FCSTD DOCUMENT  (FreeCAD 0.22R36526 (Git))
Label: card
License: All rights reserved
LicenseURL: http://en.wikipedia.org/wiki/All_rights_reserved
objects: Sketcher::SketchObject×3, PartDesign::Body×1
note: 4 computed .brp shape members not serialized (recipe doc carries the construction recipe); baked Part::Feature solids carry a one-line shape summary decoded from their .brp

FEATURE [Sketcher::SketchObject] Sketch  label="Outline"
  AttachmentSupport = -> [XY_Plane]
  FullyConstrained = true
  MapMode = 5
  sketch-geometry (10):
    g0: LineSegment StartX=-63 StartY=15 StartZ=0 EndX=-63 EndY=-15 EndZ=0
    g1: LineSegment StartX=-61 StartY=-17 StartZ=0 EndX=61 EndY=-17 EndZ=0
    g2: LineSegment StartX=63 StartY=-15 StartZ=0 EndX=63 EndY=15 EndZ=0
    g3: LineSegment StartX=61 StartY=17 StartZ=0 EndX=-61 EndY=17 EndZ=0
    g4: ArcOfCircle CenterX=-61 CenterY=15 CenterZ=0 NormalX=0 NormalY=0 NormalZ=1 AngleXU=0 Radius=2 StartAngle=1.5708 EndAngle=3.14159
    g5: ArcOfCircle CenterX=-61 CenterY=-15 CenterZ=0 NormalX=0 NormalY=0 NormalZ=1 AngleXU=0 Radius=2 StartAngle=3.14159 EndAngle=4.71239
    g6: ArcOfCircle CenterX=61 CenterY=-15 CenterZ=0 NormalX=0 NormalY=0 NormalZ=1 AngleXU=0 Radius=2 StartAngle=4.71239 EndAngle=6.28319
    g7: ArcOfCircle CenterX=61 CenterY=15 CenterZ=0 NormalX=0 NormalY=0 NormalZ=1 AngleXU=0 Radius=2 StartAngle=3.611e-13 EndAngle=1.5708
    g8: GeomPoint X=-63 Y=17 Z=0
    g9: GeomPoint X=63 Y=-17 Z=0
  constraints (23):
    c: Tangent(g0,g4) = -1.5708
    c: Tangent(g0,g5) = -1.5708
    c: Tangent(g1,g5) = -1.5708
    c: Tangent(g1,g6) = -1.5708
    c: Tangent(g2,g6) = -1.5708
    c: Tangent(g2,g7) = -1.5708
    c: Tangent(g3,g7) = -1.5708
    c: Tangent(g3,g4) = -1.5708
    c: Vertical(g0)
    c: Vertical(g2)
    c: Horizontal(g1)
    c: Horizontal(g3)
    c: Equal(g4,g5)
    c: Equal(g5,g6)
    c: Equal(g6,g7)
    c: PointOnObject(g8,g0)
    c: PointOnObject(g8,g3)
    c: PointOnObject(g9,g1)
    c: PointOnObject(g9,g2)
    c: Radius(g5) = 2
    c: DistanceX(g8,g9) = 126
    c: DistanceY(g9,g8) = 34
    c: Symmetric(g8,g9,g-1)
FEATURE [Sketcher::SketchObject] Sketch001  label="VerticalGaps"
  AttachmentSupport = -> [XY_Plane]
  FullyConstrained = false
  MapMode = 5
  sketch-geometry (9):
    g0: LineSegment StartX=-52 StartY=24.2339 StartZ=0 EndX=-52 EndY=-25.7661 EndZ=0
    g1: LineSegment StartX=-39 StartY=24.2339 StartZ=0 EndX=-39 EndY=-25.7661 EndZ=0
    g2: LineSegment StartX=-26 StartY=24.2339 StartZ=0 EndX=-26 EndY=-25.7661 EndZ=0
    g3: LineSegment StartX=-13 StartY=24.2339 StartZ=0 EndX=-13 EndY=-25.7661 EndZ=0
    g4: LineSegment StartX=0 StartY=24.2339 StartZ=0 EndX=0 EndY=-25.7661 EndZ=0
    g5: LineSegment StartX=13 StartY=24.2339 StartZ=0 EndX=13 EndY=-25.7661 EndZ=0
    g6: LineSegment StartX=26 StartY=24.2339 StartZ=0 EndX=26 EndY=-25.7661 EndZ=0
    g7: LineSegment StartX=39 StartY=24.2339 StartZ=0 EndX=39 EndY=-25.7661 EndZ=0
    g8: LineSegment StartX=52 StartY=24.2339 StartZ=0 EndX=52 EndY=-25.7661 EndZ=0
  constraints (35):
    c: Vertical(g0)
    c: Vertical(g1)
    c: Vertical(g2)
    c: Vertical(g3)
    c: DistanceY(g0,g0) = 50
    c: Equal(g0,g1)
    c: Equal(g1,g2)
    c: Equal(g2,g3)
    c: Horizontal(g0,g1)
    c: Horizontal(g1,g2)
    c: Horizontal(g2,g3)
    c: DistanceX(g0,g-1) = 52
    c: DistanceX(g1,g-1) = 39
    c: DistanceX(g2,g-1) = 26
    c: DistanceX(g3,g-1) = 13
    c: Vertical(g4)
    c: Vertical(g5)
    c: Vertical(g6)
    c: Vertical(g7)
    c: Vertical(g8)
    c: Equal(g0,g4)
    c: Equal(g4,g5)
    c: Equal(g5,g6)
    c: Equal(g6,g7)
    c: Equal(g7,g8)
    c: Horizontal(g0,g4)
    c: Horizontal(g4,g5)
    c: Horizontal(g5,g6)
    c: Horizontal(g6,g7)
    c: Horizontal(g7,g8)
    c: DistanceX(g-1,g4) = 0
    c: DistanceX(g-1,g5) = 13
    c: DistanceX(g-1,g6) = 26
    c: DistanceX(g-1,g7) = 39
    c: DistanceX(g-1,g8) = 52
FEATURE [Sketcher::SketchObject] Sketch002  label="HorizontalGaps"
  AttachmentSupport = -> [XY_Plane]
  FullyConstrained = false
  MapMode = 5
  sketch-geometry (5):
    g0: LineSegment StartX=-74.7522 StartY=-11.75 StartZ=0 EndX=75.2478 EndY=-11.75 EndZ=0
    g1: LineSegment StartX=-74.7522 StartY=-4.25 StartZ=0 EndX=75.2478 EndY=-4.25 EndZ=0
    g2: LineSegment StartX=-74.7522 StartY=4.25 StartZ=0 EndX=75.2478 EndY=4.25 EndZ=0
    g3: LineSegment StartX=-74.7522 StartY=11.75 StartZ=0 EndX=75.2478 EndY=11.75 EndZ=0
    g4: LineSegment StartX=-74.7522 StartY=0 StartZ=0 EndX=75.2478 EndY=0 EndZ=0
  constraints (19):
    c: Horizontal(g0)
    c: Horizontal(g1)
    c: Horizontal(g2)
    c: Horizontal(g3)
    c: DistanceX(g0,g0) = 150
    c: Equal(g0,g1)
    c: Equal(g1,g2)
    c: Equal(g2,g3)
    c: Vertical(g0,g1)
    c: Vertical(g1,g2)
    c: Vertical(g2,g3)
    c: PointOnObject(g4,g-1)
    c: PointOnObject(g4,g-1)
    c: Equal(g0,g4)
    c: Vertical(g0,g4)
    c: DistanceY(g0,g-1) = 11.75
    c: DistanceY(g-1,g3) = 11.75
    c: DistanceY(g1,g-1) = 4.25
    c: DistanceY(g-1,g2) = 4.25
FEATURE [PartDesign::Body] Body
  Group = -> [Sketch,Sketch001,Sketch002]
  Origin = -> Origin
